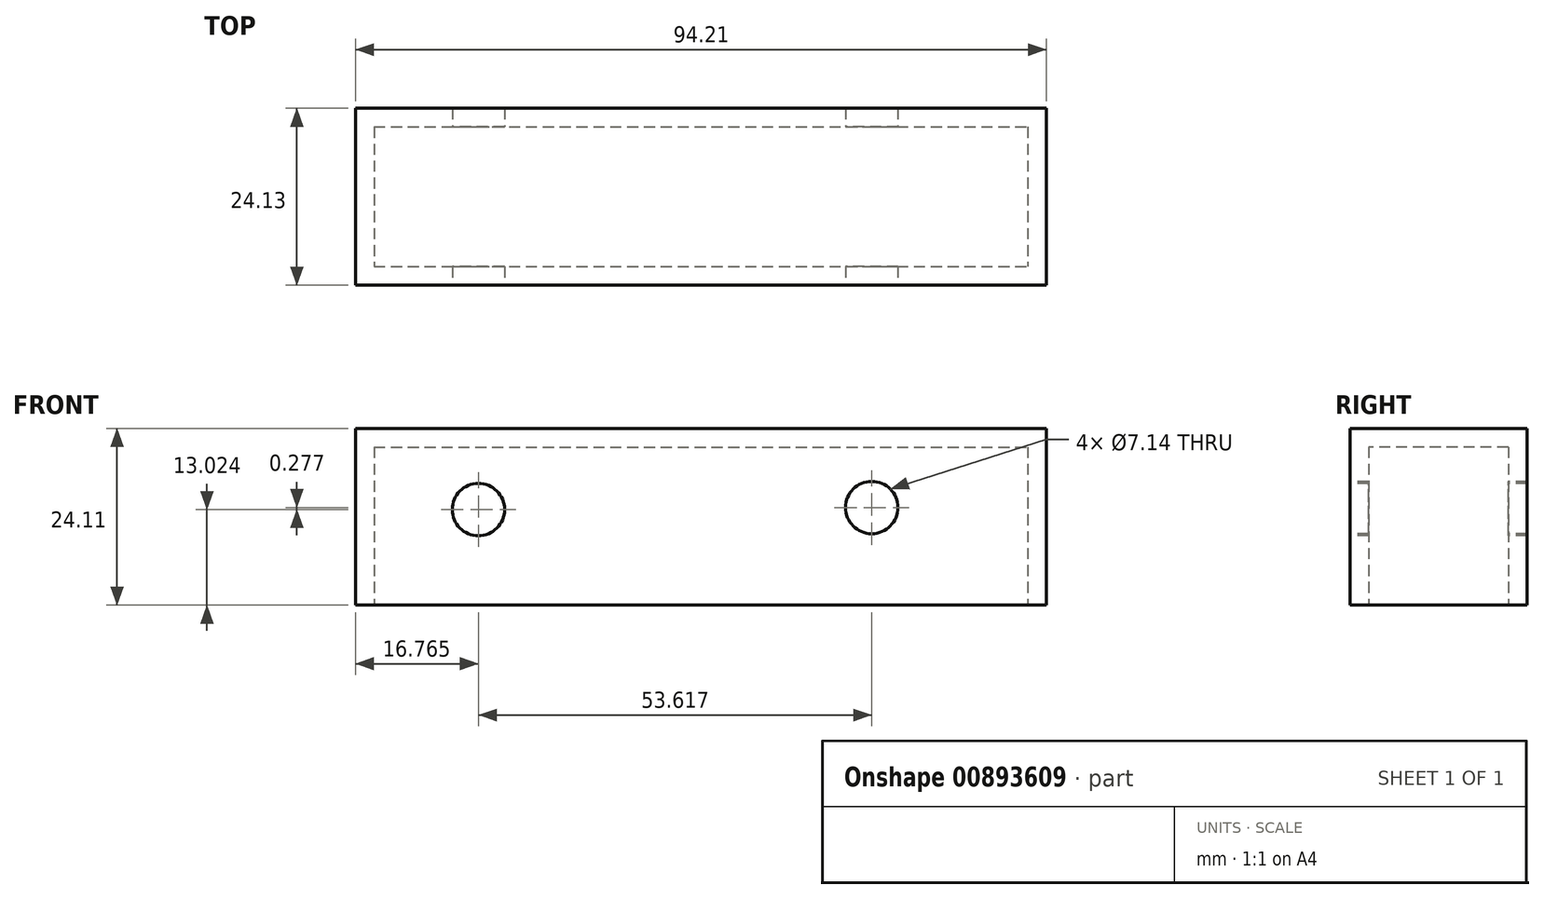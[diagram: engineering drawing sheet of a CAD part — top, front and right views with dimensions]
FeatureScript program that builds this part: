
annotation { "Feature Type Name" : "Feature", "Feature Type Description" : "" }
export const myFeature = defineFeature(function(context is Context, id is Id, definition is map)
    precondition{}
    {
        {
            var Q0;
            Q0=qCreatedBy(makeId("Front.planeOp"),FACE);
            var sketch = newSketch(context, id + "F0", { "sketchPlane" : qUnion([Q0])});
            skLineSegment(sketch, "E0.bottom", {"start": v(-39.14, 20.23) * mm, "end": v(55.07, 20.23) * mm});
            skLineSegment(sketch, "E0.top", {"start": v(-39.14, -3.88) * mm, "end": v(55.07, -3.88) * mm});
            skLineSegment(sketch, "E0.left", {"start": v(-39.14, 20.23) * mm, "end": v(-39.14, -3.88) * mm});
            skLineSegment(sketch, "E0.right", {"start": v(55.07, 20.23) * mm, "end": v(55.07, -3.88) * mm});
            skSolve(sketch);
        }
        {
            var Q0;
            Q0 = qSketchRegion(id + "F0", true);
            extrude(context, id + "F1", {"entities" : qUnion([Q0]), "oppositeDirection" : true, "depth" : 24.13 * mm, "offsetDistance" : 25.4 * mm});
        }
        {
            var Q0;
            Q0=makeQuery(id+"F1.opExtrude","SWEPT_FACE",FACE,{"disambiguationData":[OSD([sQuery(id+"F0.wireOp",EDGE,"E0.top")])]});
            shell(context, id + "F2", {"entities" : qUnion([Q0]), "thickness" : 2.54 * mm});
        }
        {
            var Q0;
            Q0=makeQuery(id+"F0.imprint","IMPRINT",FACE,{"disambiguationData":[TD([[makeQuery(id+"F0.imprint","IMPRINT",EDGE,{"derivedFrom":sQuery(id+"F0.wireOp",EDGE,"E0.bottom")}),-1.0]])]});
            var sketch = newSketch(context, id + "F3", { "sketchPlane" : qUnion([Q0])});
            skCircle(sketch, "E1", {"center": v(-22.38, 9.14) * mm, "radius": 6.69 * mm});
            skCircle(sketch, "E2", {"center": v(31.24, 9.42) * mm, "radius": 7.35 * mm});
            skSolve(sketch);
        }
        {
            var Q0;
            Q0=sQuery(id+"F3.wireOp",VERTEX,"E1.center");
            var Q1;
            Q1=sQuery(id+"F3.wireOp",VERTEX,"E2.center");
            var Q2;
            Q2=makeQuery(id+"F1.opExtrude","SWEPT_BODY",BODY,{"disambiguationData":[OSD([sQuery(id+"F0.wireOp",EDGE,"E0.bottom"),sQuery(id+"F0.wireOp",EDGE,"E0.top"),sQuery(id+"F0.wireOp",EDGE,"E0.left"),sQuery(id+"F0.wireOp",EDGE,"E0.right")])]});
            hole(context, id + "F4", {"style" : HoleStyle.SIMPLE, "endStyle" : HoleEndStyle.THROUGH, "holeDiameter" : 7.14 * mm, "majorDiameter" : 6.35 * mm, "isTappedThrough" : true, "tappedDepth" : 12.7 * mm, "tapClearance" : 3, "locations" : qUnion([Q0, Q1]), "scope" : qUnion([Q2])});
        }
    });
